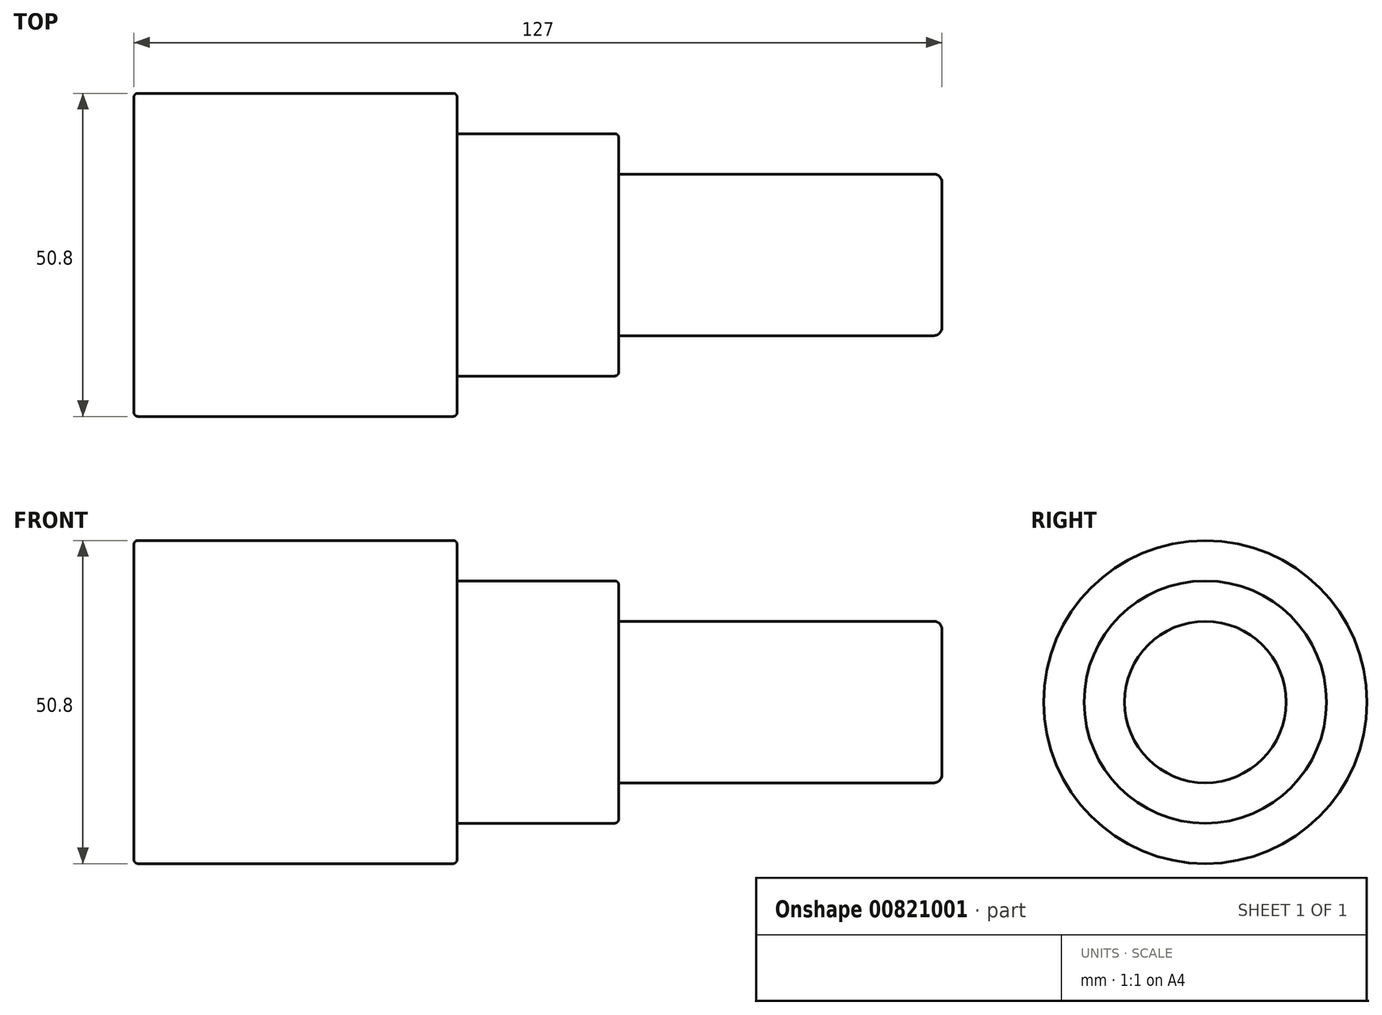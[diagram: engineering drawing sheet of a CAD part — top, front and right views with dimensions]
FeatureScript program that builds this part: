
annotation { "Feature Type Name" : "Feature", "Feature Type Description" : "" }
export const myFeature = defineFeature(function(context is Context, id is Id, definition is map)
    precondition{}
    {
        {
            var Q0;
            Q0=qCreatedBy(makeId("Front.planeOp"),FACE);
            var sketch = newSketch(context, id + "F0", { "sketchPlane" : qUnion([Q0])});
            skLineSegment(sketch, "E0", {"start": v(0, 0) * mm, "end": v(-127, 0) * mm});
            skLineSegment(sketch, "E1", {"start": v(-127, 0) * mm, "end": v(-127, 25.4) * mm});
            skLineSegment(sketch, "E2", {"start": v(-127, 25.4) * mm, "end": v(-76.2, 25.4) * mm});
            skLineSegment(sketch, "E3", {"start": v(-76.2, 25.4) * mm, "end": v(-76.2, 19.05) * mm});
            skLineSegment(sketch, "E4", {"start": v(-76.2, 19.05) * mm, "end": v(-50.8, 19.05) * mm});
            skLineSegment(sketch, "E5", {"start": v(-50.8, 19.05) * mm, "end": v(-50.8, 12.7) * mm});
            skLineSegment(sketch, "E6", {"start": v(-50.8, 12.7) * mm, "end": v(0, 12.7) * mm});
            skLineSegment(sketch, "E7", {"start": v(0, 12.7) * mm, "end": v(0, 0) * mm});
            skSolve(sketch);
        }
        {
            var Q0;
            Q0 = qSketchRegion(id + "F0", true);
            var Q1;
            Q1=sQuery(id+"F0.wireOp",EDGE,"E0");
            revolve(context, id + "F1", {"surfaceOperationType" : NewSurfaceOperationType.NEW, "entities" : qUnion([Q0]), "axis" : qUnion([Q1]), "revolveType" : RevolveType.FULL});
        }
        {
            var Q0;
            Q0=makeQuery(id+"F1.opRevolve","SWEPT_EDGE",EDGE,{"disambiguationData":[OSD([sQuery(id+"F0.wireOp",EDGE,"E6"),sQuery(id+"F0.wireOp",EDGE,"E7")])]});
            fillet(context, id + "F2", {"entities" : qUnion([Q0]), "radius" : 1.27 * mm, "tangentPropagation" : true, "allowEdgeOverflow" : false});
        }
        {
            var Q0;
            Q0=makeQuery(id+"F1.opRevolve","SWEPT_EDGE",EDGE,{"disambiguationData":[OSD([sQuery(id+"F0.wireOp",EDGE,"E4"),sQuery(id+"F0.wireOp",EDGE,"E5")])]});
            var Q1;
            Q1=makeQuery(id+"F1.opRevolve","SWEPT_EDGE",EDGE,{"disambiguationData":[OSD([sQuery(id+"F0.wireOp",EDGE,"E2"),sQuery(id+"F0.wireOp",EDGE,"E3")])]});
            var Q2;
            Q2=makeQuery(id+"F1.opRevolve","SWEPT_EDGE",EDGE,{"disambiguationData":[OSD([sQuery(id+"F0.wireOp",EDGE,"E1"),sQuery(id+"F0.wireOp",EDGE,"E2")])]});
            fillet(context, id + "F3", {"entities" : qUnion([Q0, Q1, Q2]), "radius" : 0.64 * mm, "tangentPropagation" : true, "allowEdgeOverflow" : false});
        }
    });
